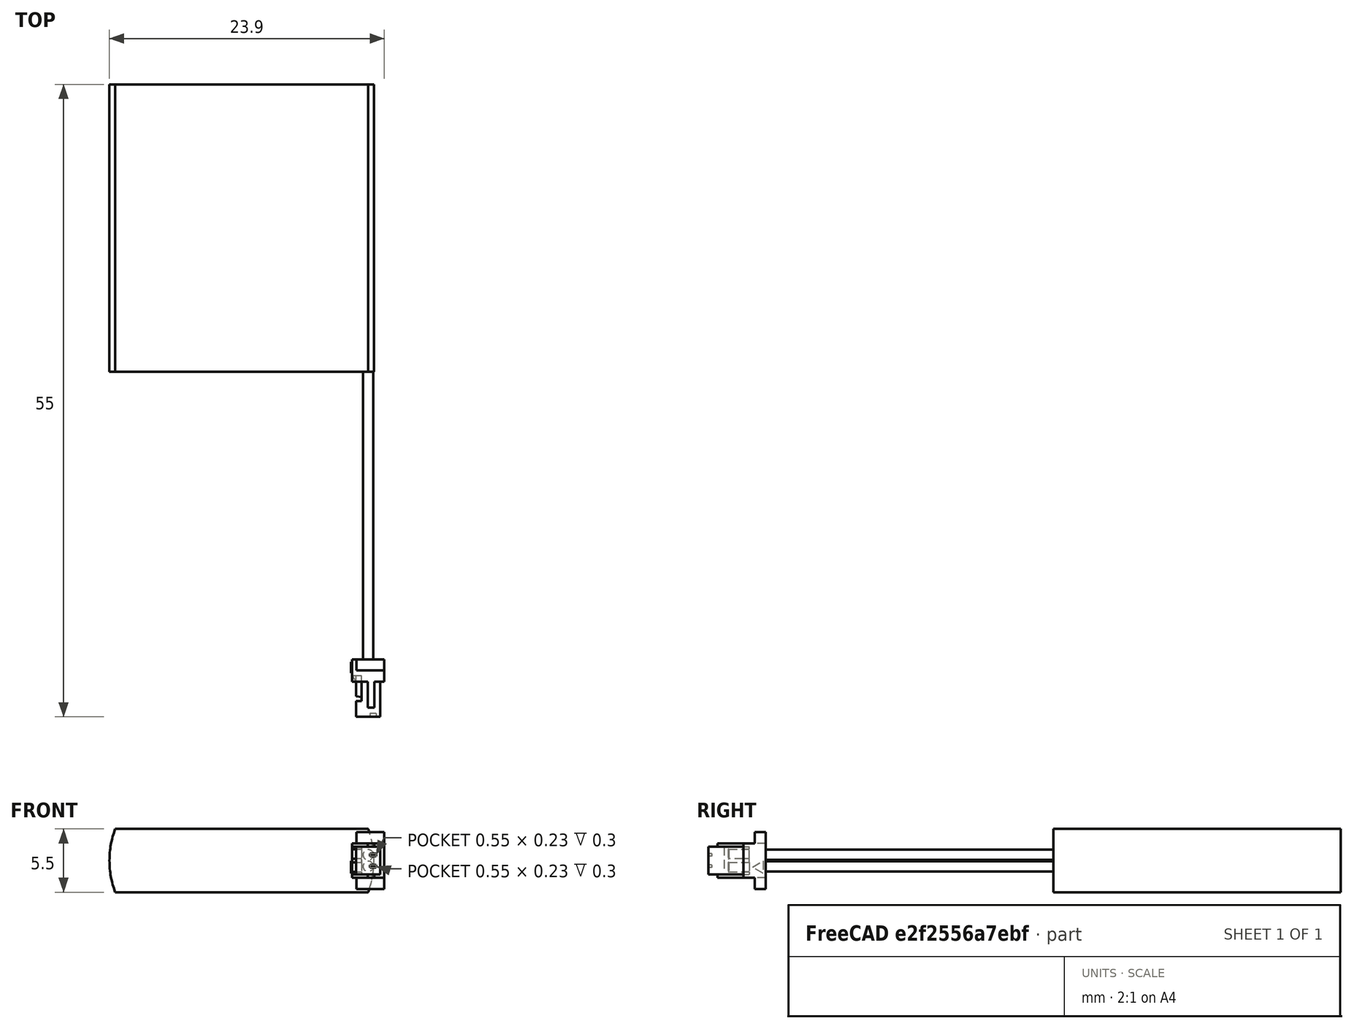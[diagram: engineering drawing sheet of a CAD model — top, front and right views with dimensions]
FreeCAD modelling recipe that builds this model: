
FCSTD DOCUMENT  (FreeCAD 2021.519R24301 +3652 (Git))
Label: ASR00007_290mAh
License: Other
objects: TechDraw::DrawViewDimension×4, Sketcher::SketchObject×3, PartDesign::Pad×3, TechDraw::DrawViewPart×2, TechDraw::DrawViewAnnotation×2, PartDesign::Pocket×1, PartDesign::Mirrored×1, PartDesign::Body×1, Part::Feature×1, Part::MultiFuse×1, TechDraw::DrawSVGTemplate×1, TechDraw::DrawPage×1, Mesh::Feature×1
note: 21 computed .brp shape members not serialized (recipe doc carries the construction recipe); baked Part::Feature solids carry a one-line shape summary decoded from their .brp

FEATURE [Sketcher::SketchObject] Sketch
  FullyConstrained = true
  MapMode = 5
  Support = -> [XY_Plane]
  sketch-geometry (4):
    g0: LineSegment StartX=-11.5 StartY=12.5 StartZ=0 EndX=11.5 EndY=12.5 EndZ=0
    g1: LineSegment StartX=11.5 StartY=12.5 StartZ=0 EndX=11.5 EndY=-12.5 EndZ=0
    g2: LineSegment StartX=11.5 StartY=-12.5 StartZ=0 EndX=-11.5 EndY=-12.5 EndZ=0
    g3: LineSegment StartX=-11.5 StartY=-12.5 StartZ=0 EndX=-11.5 EndY=12.5 EndZ=0
  constraints (10):
    c: Coincident(g0,g1)
    c: Coincident(g1,g2)
    c: Coincident(g2,g3)
    c: Coincident(g3,g0)
    c: Horizontal(g2)
    c: Vertical(g1)
    c: Symmetric(g0,g2,g-1)
    c: Symmetric(g0,g0,g-2)
    c: DistanceX(g0,g0) = 23
    c: DistanceY(g3,g3) = 25
FEATURE [PartDesign::Pad] Pad
  ClaimChildren = false
  Direction = (1,1,1)
  Fit = 0
  FitJoin = 0
  InnerFit = 0
  InnerFitJoin = 0
  InnerTaperAngle = 0
  InnerTaperAngleRev = 0
  Length = 5.5
  Length2 = 100
  Midplane = true
  NewSolid = false
  Profile = -> Sketch
  Suppress = false
  Type = 0
FEATURE [Sketcher::SketchObject] Sketch001
  ExternalGeometry = -> [Pad]
  FullyConstrained = true
  MapMode = 5
  Placement = pos=(0,12.5,0) rot=(0,0.707107,0.707107;3.14159rad)
  Support = -> [Pad]
  sketch-geometry (5):
    g0: ArcOfCircle CenterX=-3.6875 CenterY=1.5e-15 CenterZ=0 NormalX=0 NormalY=0 NormalZ=1 AngleXU=0 Radius=7.8125 StartAngle=2.78189 EndAngle=3.5013
    g1: LineSegment [constr] StartX=-11 StartY=-2.75 StartZ=0 EndX=-11 EndY=2.75 EndZ=0
    g2: LineSegment StartX=-11 StartY=-2.75 StartZ=0 EndX=-12.5 EndY=-2.75 EndZ=0
    g3: LineSegment StartX=-11 StartY=2.75 StartZ=0 EndX=-12.5 EndY=2.75 EndZ=0
    g4: LineSegment StartX=-12.5 StartY=2.75 StartZ=0 EndX=-12.5 EndY=-2.75 EndZ=0
  constraints (15):
    c: PointOnObject(g0,g-5)
    c: PointOnObject(g0,g-4)
    c: Tangent(g0,g-3)
    c: Coincident(g1,g0)
    c: Coincident(g1,g0)
    c: Vertical(g1)
    c: Coincident(g2,g0)
    c: Horizontal(g2)
    c: Coincident(g3,g0)
    c: Horizontal(g3)
    c: Coincident(g4,g3)
    c: Coincident(g4,g2)
    c: Vertical(g4)
    c: DistanceX(g3,g-4) = 1
    c: DistanceX(g-4,g0) = 0.5
FEATURE [PartDesign::Pocket] Pocket
  BaseFeature = -> Pad
  ClaimChildren = false
  Fit = 0
  FitJoin = 0
  InnerFit = 0
  InnerFitJoin = 0
  InnerTaperAngle = 0
  InnerTaperAngleRev = 0
  Length = 5
  Length2 = 100
  NewSolid = false
  Profile = -> Sketch001
  Suppress = false
  Type = 1
FEATURE [PartDesign::Mirrored] Mirrored
  BaseFeature = -> Pocket
  CopyShape = true
  MirrorPlane = -> Sketch001 [V_Axis]
  NewSolid = false
  OriginalSubs = -> [Pocket]
  Originals = -> [Pocket]
  ParallelTransform = true
  SubTransform = true
  Suppress = false
FEATURE [PartDesign::Pad] Pad001
  BaseFeature = -> Mirrored
  ClaimChildren = false
  Direction = (1,1,1)
  Fit = 0
  FitJoin = 0
  InnerFit = 0
  InnerFitJoin = 0
  InnerTaperAngle = 0
  InnerTaperAngleRev = 0
  Length = 7.85
  Length2 = 100
  NewSolid = false
  Profile = -> Mirrored [Face8]
  Reversed = true
  Suppress = false
  Type = 0
FEATURE [Sketcher::SketchObject] Sketch002
  ExternalGeometry = -> [Pad001]
  FullyConstrained = true
  MapMode = 5
  Placement = pos=(0,-12.5,0) rot=(1,0,0;1.5708rad)
  Support = -> [Pad001]
  sketch-geometry (7):
    g0: Circle CenterX=11 CenterY=-0.5 CenterZ=0 NormalX=0 NormalY=0 NormalZ=1 AngleXU=0 Radius=0.45
    g1: Circle CenterX=11 CenterY=0.5 CenterZ=0 NormalX=0 NormalY=0 NormalZ=1 AngleXU=0 Radius=0.45
    g2: LineSegment [constr] StartX=11 StartY=0.5 StartZ=0 EndX=11 EndY=-0.5 EndZ=0
    g3: GeomPoint [constr] X=11 Y=-0.95 Z=0
    g4: GeomPoint [constr] X=11 Y=0.95 Z=0
    g5: LineSegment [constr] StartX=10.55 StartY=-0.5 StartZ=0 EndX=11.45 EndY=-0.5 EndZ=0
    g6: GeomPoint [constr] X=11 Y=0.05 Z=0
  constraints (16):
    c: Coincident(g2,g1)
    c: Coincident(g2,g0)
    c: Equal(g0,g1)
    c: Diameter(g0) = 0.9
    c: Symmetric(g0,g1,g-1)
    c: PointOnObject(g3,g2)
    c: PointOnObject(g4,g1)
    c: Symmetric(g3,g4,g-1)
    c: PointOnObject(g5,g0)
    c: PointOnObject(g5,g0)
    c: Horizontal(g5)
    c: PointOnObject(g0,g5)
    c: PointOnObject(g6,g1)
    c: PointOnObject(g6,g2)
    c: DistanceX(g5,g-3) = 0.05
    c: DistanceY(g-3,g6) = 0.05
FEATURE [PartDesign::Pad] Pad002
  BaseFeature = -> Pad001
  ClaimChildren = false
  Direction = (1,1,1)
  Fit = 0
  FitJoin = 0
  InnerFit = 0
  InnerFitJoin = 0
  InnerTaperAngle = 0
  InnerTaperAngleRev = 0
  Length = 25
  Length2 = 100
  NewSolid = false
  Profile = -> Sketch002
  Suppress = false
  Type = 0
FEATURE [PartDesign::Body] Body
  AutoGroupSolids = false
  ExportMode = 0
  Group = -> [Sketch,Pad,Sketch001,Pocket,Mirrored,Pad001,Sketch002,Pad002]
  Origin = -> Origin
  Tip = -> Pad002
  _ExportChildren = -> [Pad,Pocket,Mirrored,Pad001,Pad002]
  _GroupVersion = 1
FEATURE [Part::Feature] Solid  label="Body007"
  Placement = pos=(9.71545,-39.5,6.2e-15) rot=(0,0,1;0rad)
  shape: bbox 2.9 x 5 x 4.94 mm, 60 faces (baked)
FEATURE [Part::MultiFuse] Fusion
  Shapes = -> [Body,Solid]
FEATURE [TechDraw::DrawSVGTemplate] Template
  Height = 210
  Orientation = 1
  Width = 297
FEATURE [TechDraw::DrawViewPart] View
  CoarseView = false
  Direction = (0,0,1)
  Focus = 100
  HardHidden = false
  IsoCount = 0
  IsoHidden = false
  IsoVisible = false
  LockPosition = false
  Perspective = false
  Rotation = 180
  Scale = 1.985
  ScaleType = 0
  SeamHidden = false
  SeamVisible = true
  SmoothHidden = false
  SmoothVisible = true
  Source = -> [Fusion]
  X = 178.5
  XDirection = (1,0,0)
  Y = 105
FEATURE [TechDraw::DrawViewPart] View001
  CoarseView = false
  Direction = (-1,0,0)
  Focus = 100
  HardHidden = false
  IsoCount = 0
  IsoHidden = false
  IsoVisible = false
  LockPosition = false
  Perspective = false
  Rotation = 90
  Scale = 1.985
  ScaleType = 0
  SeamHidden = false
  SeamVisible = true
  SmoothHidden = false
  SmoothVisible = true
  Source = -> [Fusion]
  X = 118.5
  XDirection = (0,-1,0)
  Y = 105
FEATURE [TechDraw::DrawViewAnnotation] Annotation
  Font = MS Shell Dlg 2
  LineSpace = 80
  LockPosition = false
  MaxWidth = -1
  Rotation = 0
  ScaleType = 0
  Text = SIDE VIEW
  TextSize = 6
  TextStyle = 0
  X = 118.5
  Y = 162
FEATURE [TechDraw::DrawViewAnnotation] Annotation001
  Font = MS Shell Dlg 2
  LineSpace = 80
  LockPosition = false
  MaxWidth = -1
  Rotation = 0
  ScaleType = 0
  Text = TOP VIEW
  TextSize = 6
  TextStyle = 0
  X = 178.5
  Y = 162
FEATURE [TechDraw::DrawViewDimension] Dimension
  Arbitrary = false
  ArbitraryTolerances = false
  EqualTolerance = true
  FormatSpec = %.1f
  FormatSpecOverTolerance = %+.1f
  FormatSpecUnderTolerance = %+.1f
  Inverted = false
  LockPosition = false
  MeasureType = 1
  OverTolerance = 3
  References2D = -> [View]
  Rotation = 0
  ScaleType = 0
  TheoreticalExact = false
  Type = 2
  UnderTolerance = -3
  X = -38
  Y = -28.5
FEATURE [TechDraw::DrawViewDimension] Dimension001
  Arbitrary = false
  ArbitraryTolerances = false
  EqualTolerance = true
  FormatSpec = %.1f
  FormatSpecOverTolerance = %+.1f
  FormatSpecUnderTolerance = %+.1f
  Inverted = false
  LockPosition = false
  MeasureType = 1
  OverTolerance = 2
  References2D = -> [View]
  Rotation = 0
  ScaleType = 0
  TheoreticalExact = false
  Type = 1
  UnderTolerance = -2
  X = 41.8932
  Y = -59
FEATURE [TechDraw::DrawViewDimension] Dimension002
  Arbitrary = false
  ArbitraryTolerances = false
  EqualTolerance = true
  FormatSpec = %.1f
  FormatSpecOverTolerance = %+.1f
  FormatSpecUnderTolerance = %+.1f
  Inverted = false
  LockPosition = false
  MeasureType = 1
  OverTolerance = 0.5
  References2D = -> [View001]
  Rotation = 0
  ScaleType = 0
  TheoreticalExact = false
  Type = 1
  UnderTolerance = -0.5
  X = -34
  Y = -59
FEATURE [TechDraw::DrawViewDimension] Dimension003
  Arbitrary = false
  ArbitraryTolerances = false
  EqualTolerance = true
  FormatSpec = %.1f
  FormatSpecOverTolerance = %+.1f
  FormatSpecUnderTolerance = %+.1f
  Inverted = false
  LockPosition = false
  MeasureType = 1
  OverTolerance = 5
  References2D = -> [View]
  Rotation = 0
  ScaleType = 0
  TheoreticalExact = false
  Type = 2
  UnderTolerance = -5
  X = -38
  Y = 21
FEATURE [TechDraw::DrawPage] Page
  KeepUpdated = true
  NextBalloonIndex = 1
  ProjectionType = 0
  Template = -> Template
  Views = -> [View,View001,Annotation,Annotation001,Dimension,Dimension001,Dimension002,Dimension003]
FEATURE [Mesh::Feature] Mesh  label="Fusion (Meshed)"
